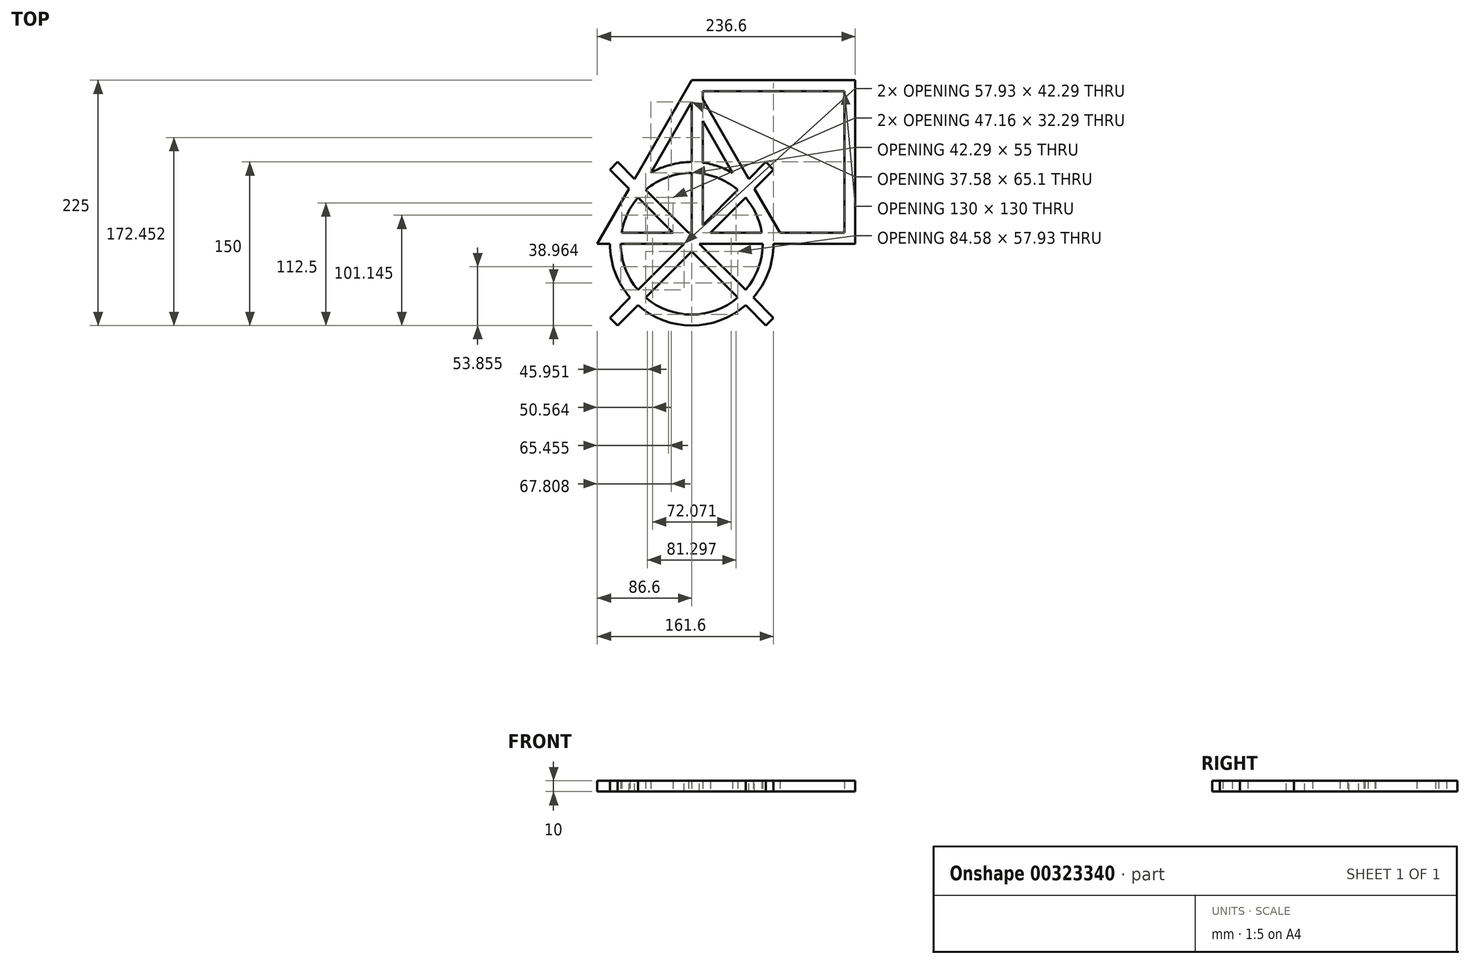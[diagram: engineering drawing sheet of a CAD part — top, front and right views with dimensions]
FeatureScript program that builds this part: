
annotation { "Feature Type Name" : "Feature", "Feature Type Description" : "" }
export const myFeature = defineFeature(function(context is Context, id is Id, definition is map)
    precondition{}
    {
        {
            var Q0;
            Q0=qCreatedBy(makeId("Top.planeOp"),FACE);
            var sketch = newSketch(context, id + "F0", { "sketchPlane" : qUnion([Q0])});
            skLineSegment(sketch, "E0.bottom", {"start": v(0, 0) * mm, "end": v(150, 0) * mm});
            skLineSegment(sketch, "E0.top", {"start": v(0, 150) * mm, "end": v(150, 150) * mm});
            skLineSegment(sketch, "E0.left", {"start": v(0, 0) * mm, "end": v(0, 150) * mm});
            skLineSegment(sketch, "E0.right", {"start": v(150, 0) * mm, "end": v(150, 150) * mm});
            skLineSegment(sketch, "E1.0", {"start": v(10, 140) * mm, "end": v(140, 140) * mm});
            skLineSegment(sketch, "E1.1", {"start": v(10, 10) * mm, "end": v(10, 140) * mm});
            skLineSegment(sketch, "E1.2", {"start": v(10, 10) * mm, "end": v(140, 10) * mm});
            skLineSegment(sketch, "E1.3", {"start": v(140, 10) * mm, "end": v(140, 140) * mm});
            skSolve(sketch);
        }
        {
            var Q0;
            Q0=makeQuery(id+"F0.imprint","IMPRINT",FACE,{"disambiguationData":[TD([[makeQuery(id+"F0.imprint","IMPRINT",EDGE,{"derivedFrom":sQuery(id+"F0.wireOp",EDGE,"E0.bottom")}),1.0]])]});
            extrude(context, id + "F1", {"entities" : qUnion([Q0]), "depth" : 10 * mm});
        }
        {
            var Q0;
            Q0=qCreatedBy(makeId("Top.planeOp"),FACE);
            var sketch = newSketch(context, id + "F2", { "sketchPlane" : qUnion([Q0])});
            skLineSegment(sketch, "E2", {"start": v(0, 0) * mm, "end": v(0, 150) * mm, "construction": true});
            skLineSegment(sketch, "E3", {"start": v(0, 150) * mm, "end": v(86.6, 0) * mm});
            skLineSegment(sketch, "E4", {"start": v(86.6, 0) * mm, "end": v(-86.6, 0) * mm});
            skLineSegment(sketch, "E5", {"start": v(-86.6, 0) * mm, "end": v(0, 150) * mm});
            skLineSegment(sketch, "E6.0", {"start": v(0, 130) * mm, "end": v(69.28, 10) * mm});
            skLineSegment(sketch, "E6.1", {"start": v(-69.28, 10) * mm, "end": v(0, 130) * mm});
            skLineSegment(sketch, "E6.2", {"start": v(69.28, 10) * mm, "end": v(-69.28, 10) * mm});
            skSolve(sketch);
        }
        {
            var Q0;
            Q0=qCreatedBy(makeId("Top.planeOp"),FACE);
            var sketch = newSketch(context, id + "F3", { "sketchPlane" : qUnion([Q0])});
            skCircle(sketch, "E7", {"center": v(0, 0) * mm, "radius": 75 * mm});
            skCircle(sketch, "E8.0", {"center": v(0, 0) * mm, "radius": 65 * mm});
            skSolve(sketch);
        }
        {
            var Q0;
            Q0=makeQuery(id+"F3.imprint","IMPRINT",FACE,{"disambiguationData":[TD([[makeQuery(id+"F3.imprint","IMPRINT",EDGE,{"derivedFrom":sQuery(id+"F3.wireOp",EDGE,"E7")}),1.0]])]});
            extrude(context, id + "F4", {"entities" : qUnion([Q0]), "depth" : 10 * mm});
        }
        {
            var Q0;
            Q0=makeQuery(id+"F2.imprint","IMPRINT",FACE,{"disambiguationData":[TD([[makeQuery(id+"F2.imprint","IMPRINT",EDGE,{"derivedFrom":sQuery(id+"F2.wireOp",EDGE,"E3")}),-1.0]])]});
            extrude(context, id + "F5", {"entities" : qUnion([Q0]), "depth" : 10 * mm});
        }
        {
            var Q0;
            Q0=qCreatedBy(makeId("Top.planeOp"),FACE);
            var sketch = newSketch(context, id + "F6", { "sketchPlane" : qUnion([Q0])});
            skLineSegment(sketch, "E9.bottom", {"start": v(75, 75) * mm, "end": v(-75, 75) * mm, "construction": true});
            skLineSegment(sketch, "E9.top", {"start": v(75, -75) * mm, "end": v(-75, -75) * mm, "construction": true});
            skLineSegment(sketch, "E9.left", {"start": v(75, 75) * mm, "end": v(75, -75) * mm, "construction": true});
            skLineSegment(sketch, "E9.right", {"start": v(-75, 75) * mm, "end": v(-75, -75) * mm, "construction": true});
            skPoint(sketch, "E9.middle", {"position": v(0, 0) * mm});
            skLineSegment(sketch, "E10", {"start": v(0, 0) * mm, "end": v(75, 75) * mm, "construction": true});
            skLineSegment(sketch, "E11", {"start": v(71.46, 71.46) * mm, "end": v(67.93, 75) * mm});
            skLineSegment(sketch, "E12", {"start": v(0, 0) * mm, "end": v(-3.54, 3.54) * mm});
            skLineSegment(sketch, "E13", {"start": v(-3.54, 3.54) * mm, "end": v(67.93, 75) * mm});
            skLineSegment(sketch, "E14.MirrorCS", {"start": v(3.54, -3.54) * mm, "end": v(75, 67.93) * mm});
            skLineSegment(sketch, "E15.MirrorCS", {"start": v(71.46, 71.46) * mm, "end": v(75, 67.93) * mm});
            skLineSegment(sketch, "E16.MirrorCS", {"start": v(0, 0) * mm, "end": v(3.54, -3.54) * mm});
            skSolve(sketch);
        }
        {
            var Q0;
            Q0=makeQuery(id+"F6.imprint","IMPRINT",FACE,{"disambiguationData":[TD([[makeQuery(id+"F6.imprint","IMPRINT",EDGE,{"derivedFrom":sQuery(id+"F6.wireOp",EDGE,"E11")}),1.0]])]});
            extrude(context, id + "F7", {"entities" : qUnion([Q0]), "depth" : 10 * mm});
        }
        {
            var Q0;
            Q0=makeQuery(id+"F7.opExtrude","SWEPT_FACE",FACE,{"disambiguationData":[OSD([sQuery(id+"F6.wireOp",EDGE,"E12"),sQuery(id+"F6.wireOp",EDGE,"E16.MirrorCS")])]});
            var sketch = newSketch(context, id + "F8", { "sketchPlane" : qUnion([Q0])});
            skLineSegment(sketch, "E17", {"start": v(0, 0) * mm, "end": v(0, 10) * mm});
            skSolve(sketch);
        }
        {
            var Q0;
            Q0=makeQuery(id+"F7.opExtrude","SWEPT_BODY",BODY,{"disambiguationData":[OSD([sQuery(id+"F6.wireOp",EDGE,"E11"),sQuery(id+"F6.wireOp",EDGE,"E12"),sQuery(id+"F6.wireOp",EDGE,"E13"),sQuery(id+"F6.wireOp",EDGE,"E14.MirrorCS"),sQuery(id+"F6.wireOp",EDGE,"E15.MirrorCS"),sQuery(id+"F6.wireOp",EDGE,"E16.MirrorCS")])]});
            var Q1;
            Q1=sQuery(id+"F8.wireOp",EDGE,"E17");
            circularPattern(context, id + "F9", {"operationType" : NewBodyOperationType.ADD, "entities" : qUnion([Q0]), "axis" : qUnion([Q1]), "angle" : 360 * degree, "instanceCount" : 4, "equalSpace" : true});
        }
    });
